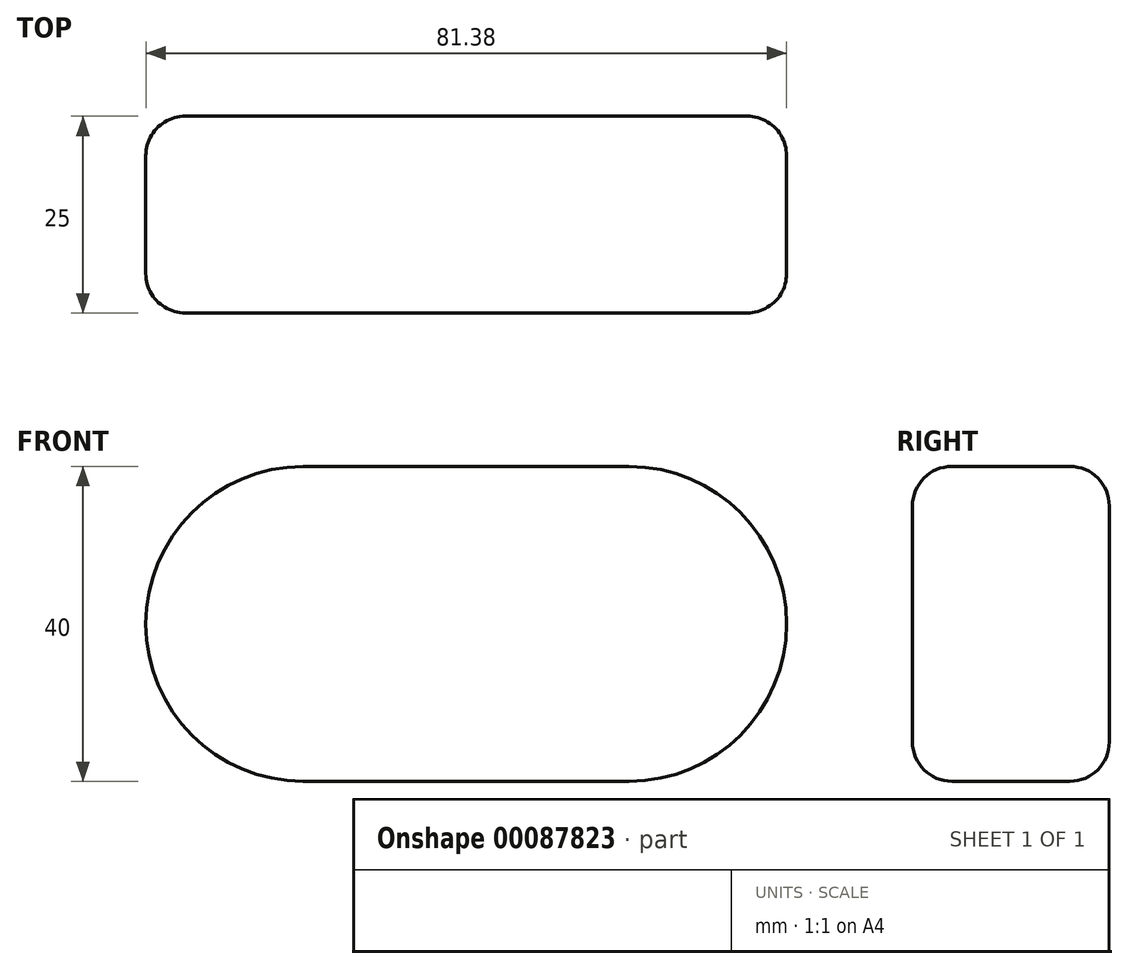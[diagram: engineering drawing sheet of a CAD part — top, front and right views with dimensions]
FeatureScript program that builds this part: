
annotation { "Feature Type Name" : "Feature", "Feature Type Description" : "" }
export const myFeature = defineFeature(function(context is Context, id is Id, definition is map)
    precondition{}
    {
        {
            var Q0;
            Q0=qCreatedBy(makeId("Front.planeOp"),FACE);
            var sketch = newSketch(context, id + "F0", { "sketchPlane" : qUnion([Q0])});
            skLineSegment(sketch, "E0", {"start": v(-18.81, 0) * mm, "end": v(22.57, 0) * mm});
            skArc(sketch, "E1.0.startCap", {"start": v(-18.81, -20) * mm, "mid": v(-38.81, 0) * mm, "end": v(-18.81, 20) * mm});
            skArc(sketch, "E1.0.endCap", {"start": v(22.57, 20) * mm, "mid": v(42.57, 0) * mm, "end": v(22.57, -20) * mm});
            skLineSegment(sketch, "E1.0.left", {"start": v(-18.81, 20) * mm, "end": v(22.57, 20) * mm});
            skLineSegment(sketch, "E1.0.right", {"start": v(-18.81, -20) * mm, "end": v(22.57, -20) * mm});
            skSolve(sketch);
        }
        {
            var Q0;
            Q0 = qSketchRegion(id + "F0", true);
            extrude(context, id + "F1", {"entities" : qUnion([Q0]), "endBound" : BoundingType.SYMMETRIC, "depth" : 25 * mm});
        }
        {
            var Q0;
            Q0=makeQuery(id+"F1.opExtrude","CAP_EDGE",EDGE,{"disambiguationData":[OSD([sQuery(id+"F0.wireOp",EDGE,"E1.0.endCap")])],"isStart":false});
            var Q1;
            Q1=makeQuery(id+"F1.opExtrude","CAP_EDGE",EDGE,{"disambiguationData":[OSD([sQuery(id+"F0.wireOp",EDGE,"E1.0.endCap")])],"isStart":true});
            fillet(context, id + "F2", {"entities" : qUnion([Q0, Q1]), "radius" : 5 * mm, "tangentPropagation" : true, "allowEdgeOverflow" : false});
        }
    });
